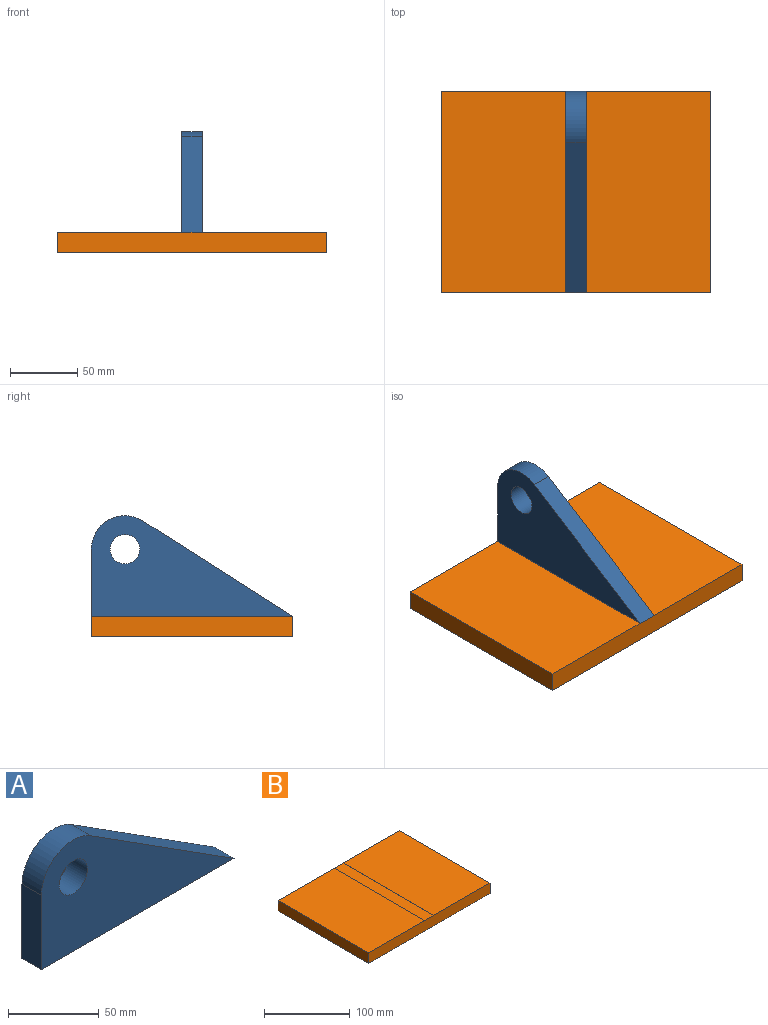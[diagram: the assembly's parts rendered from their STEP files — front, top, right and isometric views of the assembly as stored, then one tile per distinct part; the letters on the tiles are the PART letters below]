
ASSEMBLY  parts=2 mates=1
PART A: 7 faces, bbox 150x15x75 mm
  f0: cylinder r=25mm len=38.43mm, axis (0,1,0), area 801.8mm2, adj f1,f3,f5,f6
  f1: plane 50x15mm, normal (-1,0,0), area 750mm2, adj f0,f2,f5,f6
  f2: plane 150x15mm, normal (0,0,-1), area 2250mm2, adj f1,f3,f5,f6
  f3: plane 111.57x71.08mm, normal (0.54,0,0.84), area 1984.3mm2, adj f0,f2,f5,f6
  f4: cylinder r=11mm len=22mm, axis (0,1,0), area 1036.7mm2, adj f5,f6
  f5: plane 150x75mm, normal (0,-1,0), area 6316.6mm2, adj f0,f1,f2,f3,f4
  f6: plane 150x75mm, normal (0,1,0), area 6316.6mm2, adj f0,f1,f2,f3,f4
PART B: 10 faces, bbox 200x150x15 mm
  f0: plane 150x92.5mm, normal (0,0,1), area 13875mm2, adj f1,f2,f3,f7
  f1: plane 200x15mm, normal (0,1,0), area 2998.5mm2, adj f0,f3,f4,f5,f6,f7,f8,f9
  f2: plane 200x15mm, normal (0,-1,0), area 2998.5mm2, adj f0,f3,f4,f5,f6,f7,f8,f9
  f3: plane 150x15mm, normal (1,0,0), area 2250mm2, adj f0,f1,f2,f5
  f4: plane 150x15mm, normal (-1,0,0), area 2250mm2, adj f1,f2,f5,f6
  f5: plane 200x150mm, normal (0,0,-1), area 30000mm2, adj f1,f2,f3,f4
  f6: plane 150x92.5mm, normal (0,0,1), area 13875mm2, adj f1,f2,f4,f8
  f7: plane 150x0.1mm, normal (-1,0,0), area 15mm2, adj f0,f1,f2,f9
  f8: plane 150x0.1mm, normal (1,0,0), area 15mm2, adj f1,f2,f6,f9
  f9: plane 150x15mm, normal (0,0,1), area 2250mm2, adj f1,f2,f7,f8
PLACE A rot(axis=(0,0,-1),90deg) t=(20.97,3.03,75.28)mm
PLACE B t=(13.47,3.03,0.38)mm
MATE fastened B.f9 <-> A.f2  axis (0,0,1) through (13.47,3.03,0.28)mm
